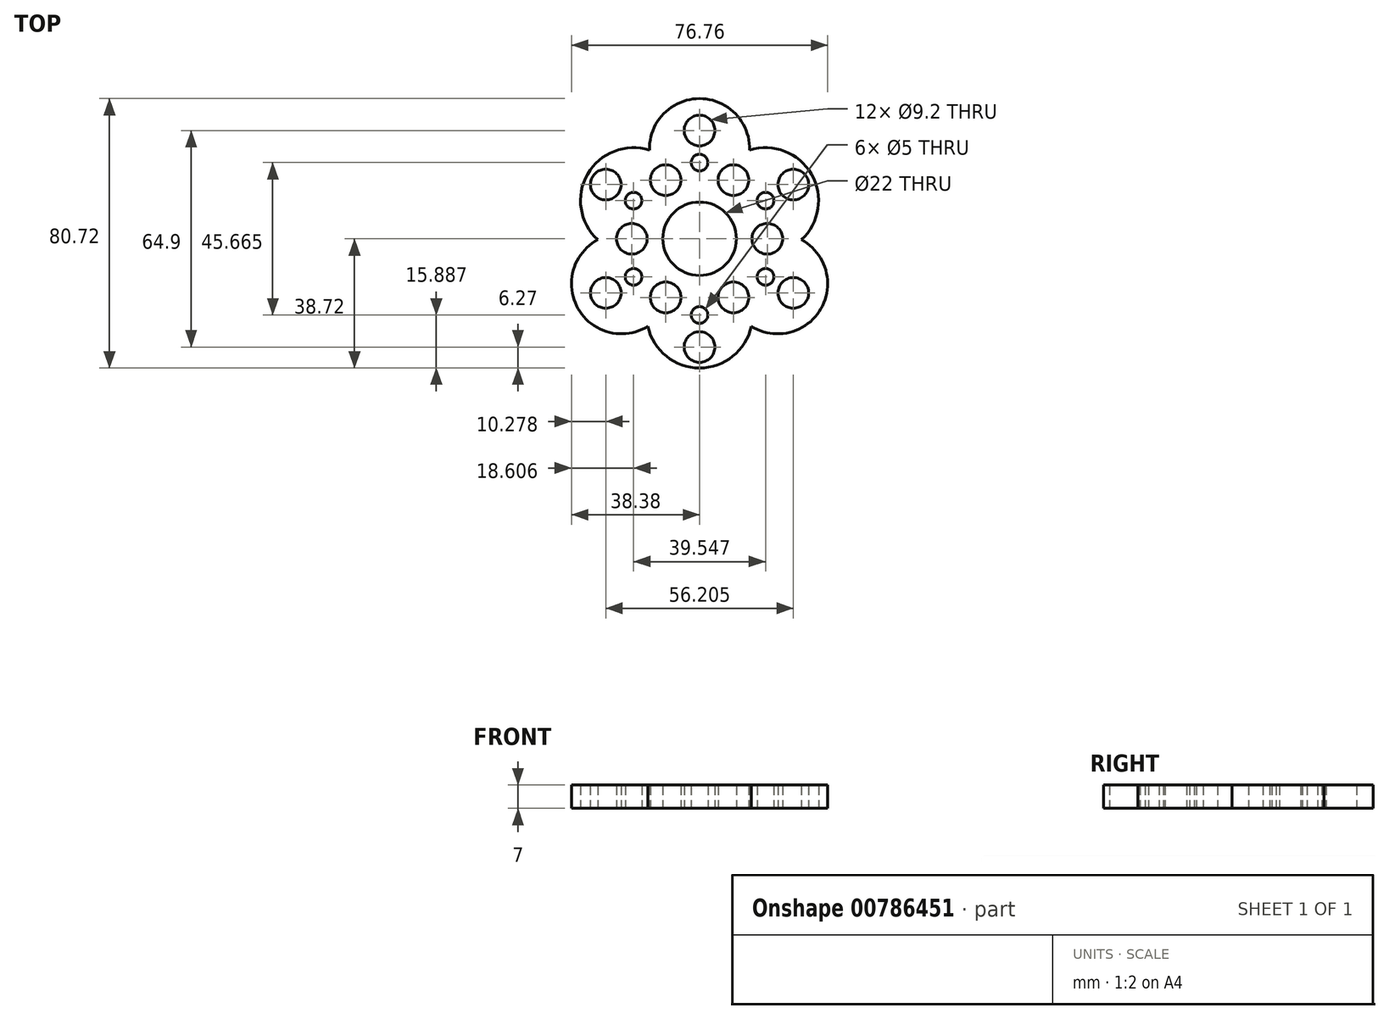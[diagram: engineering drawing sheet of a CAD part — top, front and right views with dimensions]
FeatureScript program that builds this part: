
annotation { "Feature Type Name" : "Feature", "Feature Type Description" : "" }
export const myFeature = defineFeature(function(context is Context, id is Id, definition is map)
    precondition{}
    {
        {
            var Q0;
            Q0=qCreatedBy(makeId("Top.planeOp"),FACE);
            var sketch = newSketch(context, id + "F0", { "sketchPlane" : qUnion([Q0])});
            skArc(sketch, "E0", {"start": v(9.53, 5.5) * mm, "mid": v(0, 11) * mm, "end": v(-9.53, 5.5) * mm});
            skLineSegment(sketch, "E1", {"start": v(0, 0) * mm, "end": v(0, 11) * mm});
            skArc(sketch, "E2", {"start": v(21.94, 12.67) * mm, "mid": v(18.52, 13.58) * mm, "end": v(17.6, 10.17) * mm});
            skArc(sketch, "E3", {"start": v(33.53, 19.36) * mm, "mid": v(25.53, 26.22) * mm, "end": v(15, 26.57) * mm});
            skArc(sketch, "E4.MirrorCS", {"start": v(-33.53, 19.36) * mm, "mid": v(-25.53, 26.22) * mm, "end": v(-15, 26.57) * mm});
            skPoint(sketch, "E5.orphan", {"position": v(46.77, 27) * mm});
            skPoint(sketch, "E6.orphan", {"position": v(-6.02, 3.47) * mm});
            skArc(sketch, "E7.trimOffspring", {"start": v(15, 26.57) * mm, "mid": v(0, 42) * mm, "end": v(-15, 26.57) * mm});
            skPoint(sketch, "E8.trimOffspring.end.orphan", {"position": v(6.02, 3.47) * mm});
            skPoint(sketch, "E9.orphan", {"position": v(-46.77, 27) * mm});
            skArc(sketch, "E10.1.1", {"start": v(-30.5, -0.3) * mm, "mid": v(-36.37, -21) * mm, "end": v(-15.5, -26.27) * mm});
            skArc(sketch, "E10.1.2", {"start": v(0, -38.72) * mm, "mid": v(-9.94, -35.22) * mm, "end": v(-15.5, -26.27) * mm});
            skArc(sketch, "E10.1.6", {"start": v(-9.53, 5.5) * mm, "mid": v(-9.53, -5.5) * mm, "end": v(0, -11) * mm});
            skArc(sketch, "E10.1.9", {"start": v(-33.53, 19.36) * mm, "mid": v(-35.47, 9) * mm, "end": v(-30.5, -0.3) * mm});
            skArc(sketch, "E10.2.1", {"start": v(15.5, -26.27) * mm, "mid": v(36.37, -21) * mm, "end": v(30.5, -0.3) * mm});
            skArc(sketch, "E10.2.2", {"start": v(33.53, 19.36) * mm, "mid": v(35.47, 9) * mm, "end": v(30.5, -0.3) * mm});
            skArc(sketch, "E10.2.4", {"start": v(21.94, 12.67) * mm, "mid": v(21.02, 9.25) * mm, "end": v(17.6, 10.17) * mm});
            skArc(sketch, "E10.2.6", {"start": v(0, -11) * mm, "mid": v(9.53, -5.5) * mm, "end": v(9.53, 5.5) * mm});
            skArc(sketch, "E10.2.9", {"start": v(0, -38.72) * mm, "mid": v(9.94, -35.22) * mm, "end": v(15.5, -26.27) * mm});
            skPoint(sketch, "E11.orphan", {"position": v(-8.42, -12.41) * mm});
            skPoint(sketch, "E12.orphan", {"position": v(14.96, -1.09) * mm});
            skCircle(sketch, "E13", {"center": v(28.1, 16.23) * mm, "radius": 4.6 * mm});
            skCircle(sketch, "E14.1.0", {"center": v(0, 32.45) * mm, "radius": 4.6 * mm});
            skArc(sketch, "E14.1.1", {"start": v(0, 25.33) * mm, "mid": v(2.5, 22.83) * mm, "end": v(0, 20.33) * mm});
            skArc(sketch, "E14.1.2", {"start": v(0, 25.33) * mm, "mid": v(-2.5, 22.83) * mm, "end": v(0, 20.33) * mm});
            skCircle(sketch, "E14.2.0", {"center": v(-28.1, 16.23) * mm, "radius": 4.6 * mm});
            skArc(sketch, "E14.2.1", {"start": v(-21.94, 12.67) * mm, "mid": v(-18.52, 13.58) * mm, "end": v(-17.6, 10.17) * mm});
            skArc(sketch, "E14.2.2", {"start": v(-21.94, 12.67) * mm, "mid": v(-21.02, 9.25) * mm, "end": v(-17.6, 10.17) * mm});
            skCircle(sketch, "E14.3.0", {"center": v(-28.1, -16.23) * mm, "radius": 4.6 * mm});
            skArc(sketch, "E14.3.1", {"start": v(-21.94, -12.67) * mm, "mid": v(-21.02, -9.25) * mm, "end": v(-17.6, -10.17) * mm});
            skArc(sketch, "E14.3.2", {"start": v(-21.94, -12.67) * mm, "mid": v(-18.52, -13.58) * mm, "end": v(-17.6, -10.17) * mm});
            skCircle(sketch, "E14.4.0", {"center": v(0, -32.45) * mm, "radius": 4.6 * mm});
            skArc(sketch, "E14.4.1", {"start": v(0, -25.33) * mm, "mid": v(-2.5, -22.83) * mm, "end": v(0, -20.33) * mm});
            skArc(sketch, "E14.4.2", {"start": v(0, -25.33) * mm, "mid": v(2.5, -22.83) * mm, "end": v(0, -20.33) * mm});
            skCircle(sketch, "E14.5.0", {"center": v(28.1, -16.23) * mm, "radius": 4.6 * mm});
            skArc(sketch, "E14.5.1", {"start": v(21.94, -12.67) * mm, "mid": v(18.52, -13.58) * mm, "end": v(17.6, -10.17) * mm});
            skArc(sketch, "E14.5.2", {"start": v(21.94, -12.67) * mm, "mid": v(21.02, -9.25) * mm, "end": v(17.6, -10.17) * mm});
            skCircle(sketch, "E15", {"center": v(20.3, 0) * mm, "radius": 4.6 * mm});
            skCircle(sketch, "E16.1.0", {"center": v(10.15, 17.57) * mm, "radius": 4.6 * mm});
            skCircle(sketch, "E16.2.0", {"center": v(-10.15, 17.57) * mm, "radius": 4.6 * mm});
            skCircle(sketch, "E16.3.0", {"center": v(-20.3, 0) * mm, "radius": 4.6 * mm});
            skCircle(sketch, "E16.4.0", {"center": v(-10.15, -17.57) * mm, "radius": 4.6 * mm});
            skCircle(sketch, "E16.5.0", {"center": v(10.15, -17.57) * mm, "radius": 4.6 * mm});
            skSolve(sketch);
        }
        {
            var Q0;
            Q0 = qSketchRegion(id + "F0", true);
            extrude(context, id + "F1", {"entities" : qUnion([Q0]), "depth" : 7 * mm, "offsetDistance" : 25 * mm});
        }
    });
